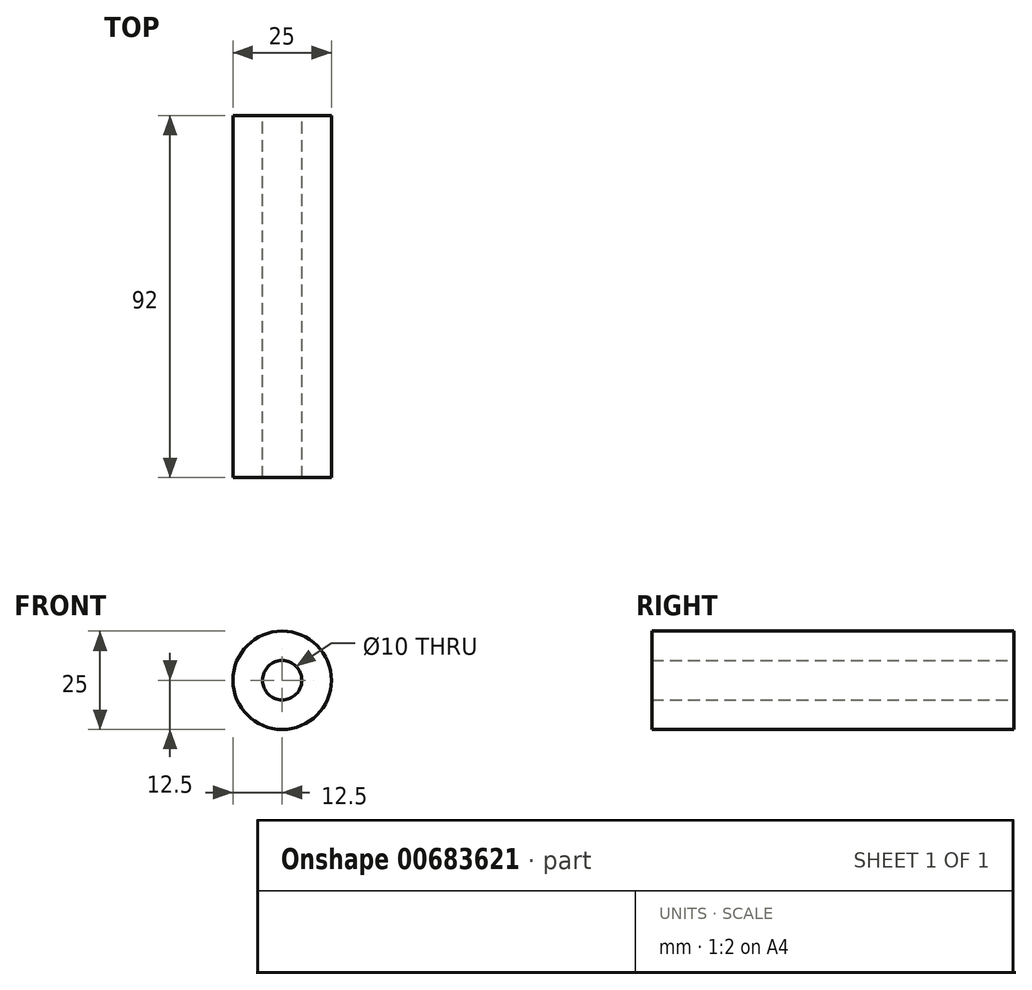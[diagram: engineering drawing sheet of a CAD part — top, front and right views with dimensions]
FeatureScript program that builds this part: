
annotation { "Feature Type Name" : "Feature", "Feature Type Description" : "" }
export const myFeature = defineFeature(function(context is Context, id is Id, definition is map)
    precondition{}
    {
        {
            var Q0;
            Q0=qCreatedBy(makeId("Front.planeOp"),FACE);
            var sketch = newSketch(context, id + "F0", { "sketchPlane" : qUnion([Q0])});
            skCircle(sketch, "E0", {"center": v(0, 0) * mm, "radius": 12.5 * mm});
            skCircle(sketch, "E1", {"center": v(0, 0) * mm, "radius": 5 * mm});
            skSolve(sketch);
        }
        {
            var Q0;
            Q0 = qSketchRegion(id + "F0", true);
            extrude(context, id + "F1", {"entities" : qUnion([Q0]), "depth" : 92 * mm, "offsetDistance" : 25 * mm});
        }
    });
